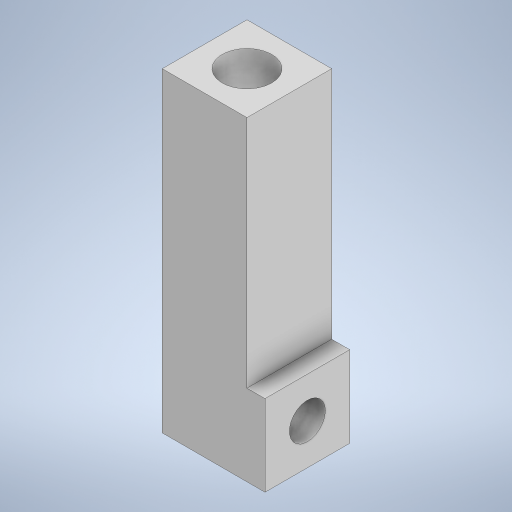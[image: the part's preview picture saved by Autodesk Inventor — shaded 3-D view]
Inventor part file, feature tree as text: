
AUTODESK INVENTOR PART (.ipt)
format: ipt  version: 2024.2 (Build 282272000, 272)  size: 243,200 bytes
history: native  units: mm
features: extrude x4, sketch x4
ambient origin geometry x8: Origin, YZ Plane, XZ Plane, XY Plane, X Axis, Y Axis, Z Axis, Center Point
bodies: Solid1 (feature_tree)
feature tree (8):
  extrude  "Extrusion1"  Depth=9.4mm
  extrude  "Extrusion2"  Depth=35.0mm
  extrude  "Extrusion3"  Depth=4.0mm
  extrude  "Extrusion4"  Depth=2.0mm TaperAngle=0.0deg
  sketch  "Sketch1"  dims[d0=9.4mm d1=9.4mm]
  sketch  "Sketch2"  dims[d2=35.0mm d3=0.0mm d4=5.5mm]
  sketch  "Sketch3"  dims[d5=30.0mm d6=0.0mm d7=4.0mm]
  sketch  "Sketch4"  dims[d8=4.5mm d9=5.0mm d10=0.0mm d11=9.0mm d12=2.0mm d13=0.0mm]
